# Revit family: DTG36M955F_Revit
name_source: partatom
category: Specialty Equipment
revit_build: Autodesk Revit MEP 2014 (Build: 20130308_1515(x64)
units: mm (PartAtom-declared; Revit-internal decimal feet)

## types (1)
- DTG36M955F
    AUTOMATIC REIGNITION = YES
    Adjustment = Stainless Steel
    Burner = Stainless Steel
    CENTER BURNER POWER (BTU) = 18,500 (DUAL BURNER)
    CIRCUIT BREAKER (A) = 15
    CONTROL LOCATION = RIGHT
    DISHWASHER SAFE KNOBS = YES
    Depth = 21"
    Description = 36-INCH GAS COOKTOP MODERNIST COLLECTION
    ENERGY SOURCE = GAS AND ELECTRIC
    FREQUENCY (HZ) = 60
    GAS TYPE = NATURAL GAS
    Height = 6 1/2"
    INSTALLATION TYPE = LOW-PROFILE (FLUSH)
    LED KNOB BACKLIGHT + INDICATOR = YES
    LEFT FRONT BURNER (BTU) = 13,000 (STACK BURNER)
    LEFT REAR BURNER (BTU) = 13,000 (STACK BURNER)
    LIMITED, PARTS AND LABOR = 1 YEAR
    LP CONVERSION KIT = YES
    Manufacturer = Dacor
    Model = DTG36M955F
    RIGHT FRONT BURNER (BTU) = 9,500 (STACK BURNER)
    RIGHT REAR BURNER (BTU) = 9,500 (STACK BURNER)
    SEALED BURNERS = YES
    Support = Plastic-Black
    TOTAL NUMBER OF COOKTOP BURNERS = 5 (BRASS)
    Unit = Stainless Steel
    VOLTS (V) = 120
    WI FI HOOD CONNECTIVITY = YES
    Width = 36"

## geometry (parser evidence)
native form markers: Sweep x1
no freeform markers — native parametric forms only
